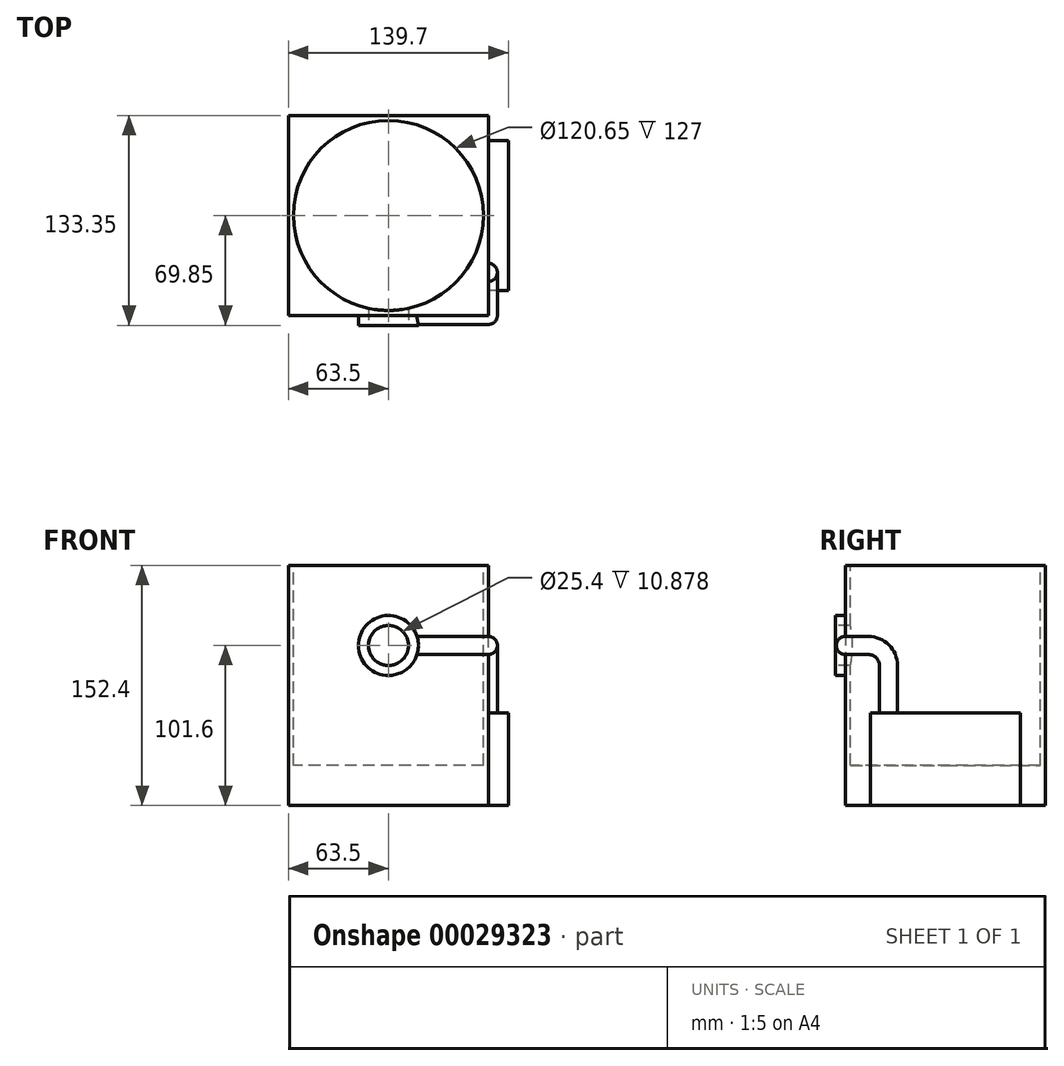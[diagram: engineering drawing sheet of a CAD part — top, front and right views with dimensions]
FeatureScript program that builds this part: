
annotation { "Feature Type Name" : "Feature", "Feature Type Description" : "" }
export const myFeature = defineFeature(function(context is Context, id is Id, definition is map)
    precondition{}
    {
        {
            var Q0;
            Q0=qCreatedBy(makeId("Top.planeOp"),FACE);
            var sketch = newSketch(context, id + "F0", { "sketchPlane" : qUnion([Q0])});
            skLineSegment(sketch, "E0.rect.bottom", {"start": v(63.5, 63.5) * mm, "end": v(-63.5, 63.5) * mm});
            skLineSegment(sketch, "E0.rect.top", {"start": v(63.5, -63.5) * mm, "end": v(-63.5, -63.5) * mm});
            skLineSegment(sketch, "E0.rect.left", {"start": v(63.5, 63.5) * mm, "end": v(63.5, -63.5) * mm});
            skLineSegment(sketch, "E0.rect.right", {"start": v(-63.5, 63.5) * mm, "end": v(-63.5, -63.5) * mm});
            skPoint(sketch, "E0.rect.middle", {"position": v(0, 0) * mm});
            skSolve(sketch);
        }
        {
            var Q0;
            Q0 = qSketchRegion(id + "F0", true);
            extrude(context, id + "F1", {"entities" : qUnion([Q0]), "depth" : 152.4 * mm});
        }
        {
            var Q0;
            Q0=makeQuery(id+"F1.opExtrude","CAP_FACE",FACE,{"disambiguationData":[OSD([sQuery(id+"F0.wireOp",EDGE,"E0.rect.bottom"),sQuery(id+"F0.wireOp",EDGE,"E0.rect.top"),sQuery(id+"F0.wireOp",EDGE,"E0.rect.left"),sQuery(id+"F0.wireOp",EDGE,"E0.rect.right")])],"isStart":false});
            var sketch = newSketch(context, id + "F2", { "sketchPlane" : qUnion([Q0])});
            skCircle(sketch, "E1", {"center": v(0, 0) * mm, "radius": 60.33 * mm});
            skSolve(sketch);
        }
        {
            var Q0;
            Q0 = qSketchRegion(id + "F2", true);
            extrude(context, id + "F3", {"entities" : qUnion([Q0]), "operationType" : NewBodyOperationType.REMOVE, "oppositeDirection" : true, "depth" : 127 * mm});
        }
        {
            var Q0;
            Q0=makeQuery(id+"F1.opExtrude","SWEPT_FACE",FACE,{"disambiguationData":[OSD([sQuery(id+"F0.wireOp",EDGE,"E0.rect.top")])]});
            var sketch = newSketch(context, id + "F4", { "sketchPlane" : qUnion([Q0])});
            skCircle(sketch, "E2", {"center": v(0, 101.6) * mm, "radius": 12.7 * mm});
            skSolve(sketch);
        }
        {
            var Q0;
            Q0 = qSketchRegion(id + "F4", true);
            extrude(context, id + "F5", {"entities" : qUnion([Q0]), "operationType" : NewBodyOperationType.REMOVE, "endBound" : BoundingType.UP_TO_NEXT, "oppositeDirection" : true, "depth" : 25.4 * mm});
        }
        {
            var Q0;
            Q0=makeQuery(id+"F1.opExtrude","SWEPT_FACE",FACE,{"disambiguationData":[OSD([sQuery(id+"F0.wireOp",EDGE,"E0.rect.top")])]});
            var sketch = newSketch(context, id + "F6", { "sketchPlane" : qUnion([Q0])});
            skCircle(sketch, "E3", {"center": v(0, 101.6) * mm, "radius": 12.7 * mm});
            skCircle(sketch, "E4", {"center": v(0, 101.6) * mm, "radius": 19.05 * mm});
            skSolve(sketch);
        }
        {
            var Q0;
            Q0 = qSketchRegion(id + "F6", true);
            extrude(context, id + "F7", {"entities" : qUnion([Q0]), "operationType" : NewBodyOperationType.ADD, "depth" : 6.35 * mm});
        }
        {
            var Q0;
            Q0=makeQuery(id+"F1.opExtrude","SWEPT_FACE",FACE,{"disambiguationData":[OSD([sQuery(id+"F0.wireOp",EDGE,"E0.rect.left")])]});
            var sketch = newSketch(context, id + "F8", { "sketchPlane" : qUnion([Q0])});
            skLineSegment(sketch, "E5.bottom", {"start": v(47.63, 0) * mm, "end": v(-47.62, 0) * mm});
            skLineSegment(sketch, "E5.top", {"start": v(47.63, 58.83) * mm, "end": v(-47.63, 58.83) * mm});
            skLineSegment(sketch, "E5.left", {"start": v(47.63, 0) * mm, "end": v(47.63, 58.83) * mm});
            skLineSegment(sketch, "E5.right", {"start": v(-47.62, 0) * mm, "end": v(-47.63, 58.83) * mm});
            skSolve(sketch);
        }
        {
            var Q0;
            Q0 = qSketchRegion(id + "F8", true);
            extrude(context, id + "F9", {"entities" : qUnion([Q0]), "operationType" : NewBodyOperationType.ADD, "depth" : 12.7 * mm});
        }
        {
            var Q0;
            Q0=makeQuery(id+"F1.opExtrude","SWEPT_FACE",FACE,{"disambiguationData":[OSD([sQuery(id+"F0.wireOp",EDGE,"E0.rect.left")])]});
            var sketch = newSketch(context, id + "F10", { "sketchPlane" : qUnion([Q0])});
            skArc(sketch, "E6", {"start": v(-63.5, 107.31) * mm, "mid": v(-69.22, 101.6) * mm, "end": v(-63.5, 95.88) * mm});
            skLineSegment(sketch, "E7", {"start": v(-63.5, 107.31) * mm, "end": v(-63.5, 95.88) * mm});
            skSolve(sketch);
        }
        {
            var Q0;
            Q0 = qSketchRegion(id + "F10", true);
            extrude(context, id + "F11", {"entities" : qUnion([Q0]), "endBound" : BoundingType.UP_TO_NEXT, "oppositeDirection" : true, "depth" : 25.4 * mm});
        }
        {
            var Q0;
            Q0=makeQuery(id+"F9.opExtrude","SWEPT_FACE",FACE,{"disambiguationData":[OSD([sQuery(id+"F8.wireOp",EDGE,"E5.top")])]});
            var sketch = newSketch(context, id + "F12", { "sketchPlane" : qUnion([Q0])});
            skArc(sketch, "E8", {"start": v(63.5, -41.86) * mm, "mid": v(69.22, -36.15) * mm, "end": v(63.5, -30.43) * mm});
            skLineSegment(sketch, "E9", {"start": v(63.5, -30.43) * mm, "end": v(63.5, -41.86) * mm});
            skSolve(sketch);
        }
        {
            var Q0;
            Q0=makeQuery(id+"F1.opExtrude","SWEPT_FACE",FACE,{"disambiguationData":[OSD([sQuery(id+"F0.wireOp",EDGE,"E0.rect.left")])]});
            var sketch = newSketch(context, id + "F13", { "sketchPlane" : qUnion([Q0])});
            skLineSegment(sketch, "E10", {"start": v(-36.15, 58.83) * mm, "end": v(-36.15, 88.9) * mm});
            skLineSegment(sketch, "E11", {"start": v(-63.5, 101.6) * mm, "end": v(-48.85, 101.6) * mm});
            skArc(sketch, "E12.filletArc", {"start": v(-36.15, 88.9) * mm, "mid": v(-39.87, 97.88) * mm, "end": v(-48.85, 101.6) * mm});
            skSolve(sketch);
        }
        {
            var Q0;
            Q0=makeQuery(id+"F12.imprint","IMPRINT",FACE,{"disambiguationData":[TD([[makeQuery(id+"F12.imprint","IMPRINT",EDGE,{"derivedFrom":sQuery(id+"F12.wireOp",EDGE,"E8")}),1.0]])]});
            var Q1;
            Q1=sQuery(id+"F13.wireOp",EDGE,"E10");
            var Q2;
            Q2=sQuery(id+"F13.wireOp",EDGE,"E12.filletArc");
            var Q3;
            Q3=sQuery(id+"F13.wireOp",EDGE,"E11");
            sweep(context, id + "F14", {"operationType" : NewBodyOperationType.ADD, "profiles" : qUnion([Q0]), "path" : qUnion([Q1, Q2, Q3])});
        }
        {
            var Q0;
            Q0=makeQuery(id+"F14.opSweep","CAP_FACE",FACE,{"disambiguationData":[OSD([sQuery(id+"F12.wireOp",EDGE,"E8"),sQuery(id+"F12.wireOp",EDGE,"E9"),sQuery(id+"F13.wireOp",VERTEX,"E11.start")])],"isStart":false});
            var Q1;
            Q1=makeQuery(id+"F14.opSweep","CAP_EDGE",EDGE,{"disambiguationData":[OSD([sQuery(id+"F12.wireOp",EDGE,"E9"),sQuery(id+"F13.wireOp",VERTEX,"E11.start")])],"isStart":false});
            revolve(context, id + "F15", {"operationType" : NewBodyOperationType.ADD, "entities" : qUnion([Q0]), "axis" : qUnion([Q1]), "revolveType" : RevolveType.ONE_DIRECTION, "angle" : 90 * degree});
        }
    });
